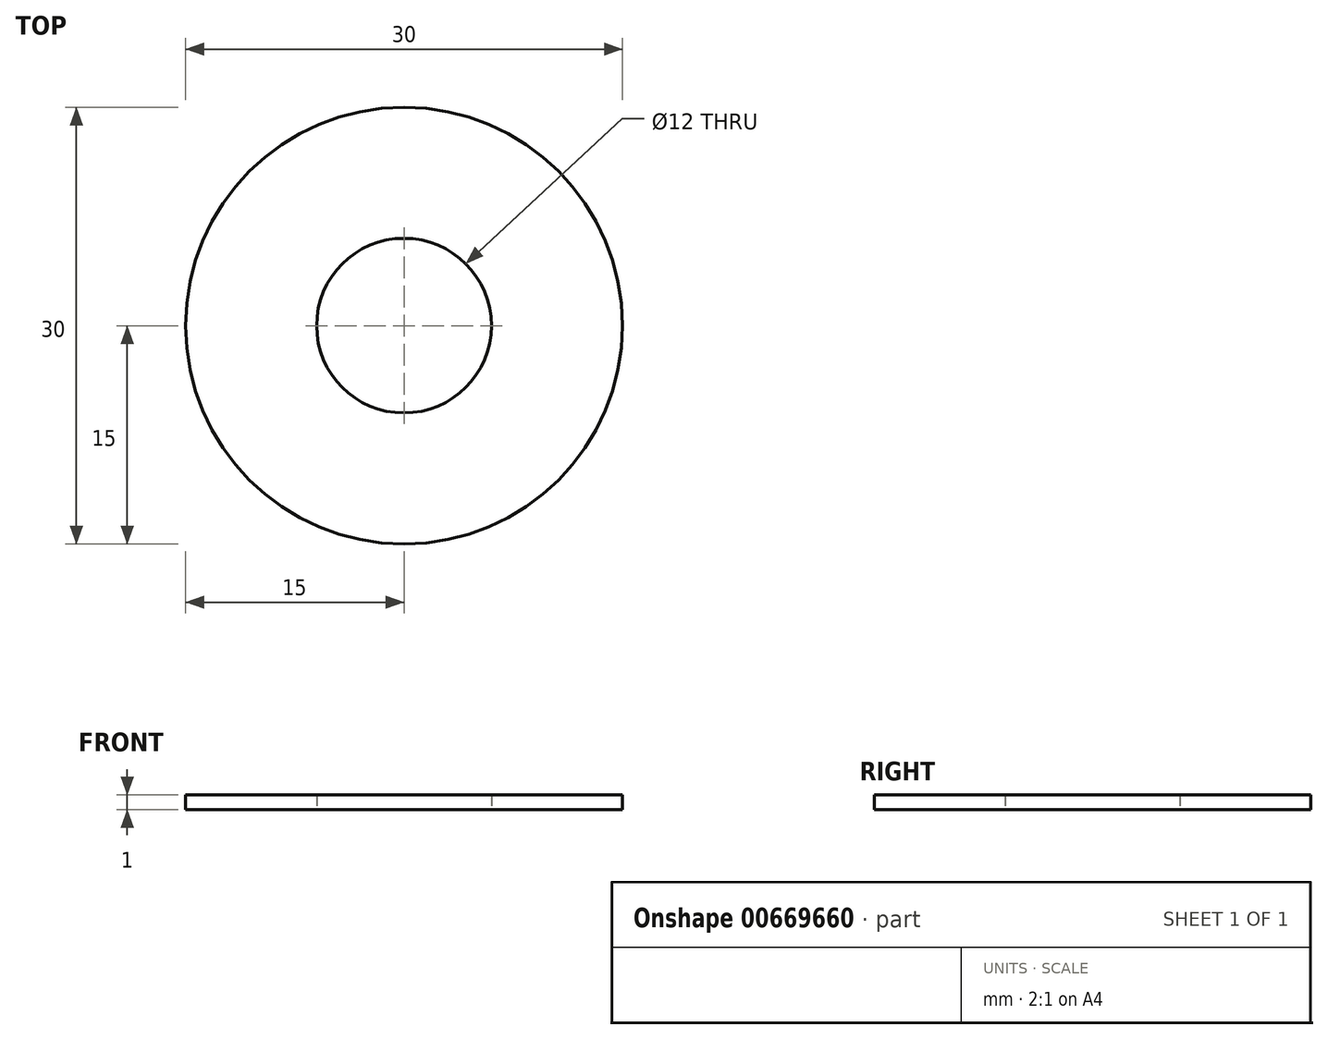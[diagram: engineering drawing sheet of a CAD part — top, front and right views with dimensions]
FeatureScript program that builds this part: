
annotation { "Feature Type Name" : "Feature", "Feature Type Description" : "" }
export const myFeature = defineFeature(function(context is Context, id is Id, definition is map)
    precondition{}
    {
        {
            var Q0;
            Q0=qCreatedBy(makeId("Top.planeOp"),FACE);
            var sketch = newSketch(context, id + "F0", { "sketchPlane" : qUnion([Q0])});
            skCircle(sketch, "E0", {"center": v(0, 0) * mm, "radius": 15 * mm});
            skCircle(sketch, "E1", {"center": v(0, 0) * mm, "radius": 6 * mm});
            skSolve(sketch);
        }
        {
            var Q0;
            Q0 = qSketchRegion(id + "F0", true);
            extrude(context, id + "F1", {"entities" : qUnion([Q0]), "depth" : 1 * mm, "offsetDistance" : 25 * mm});
        }
    });
